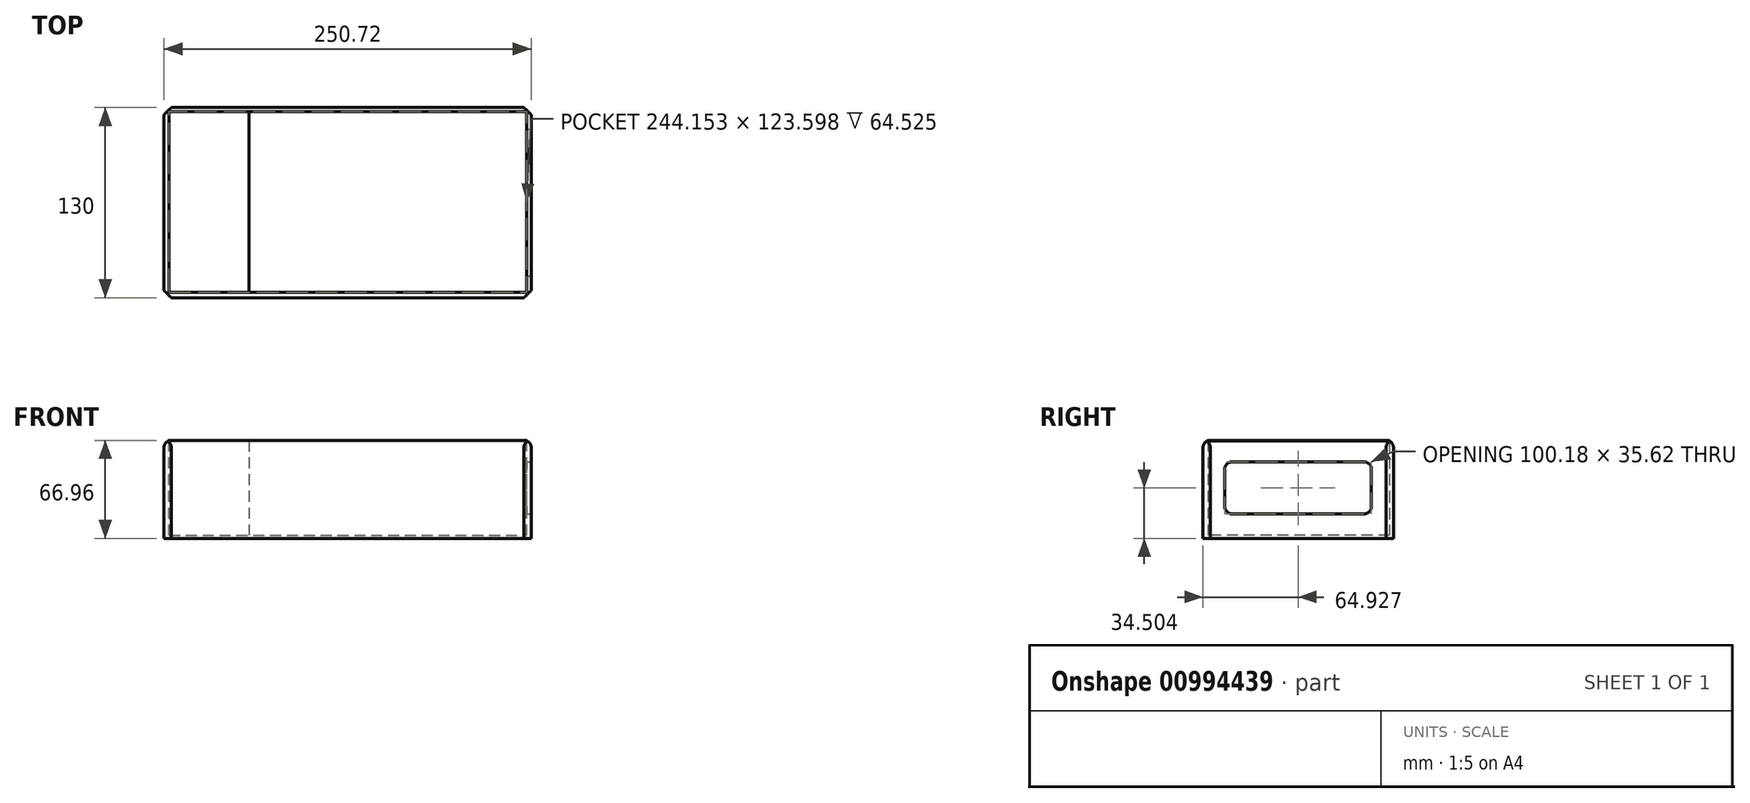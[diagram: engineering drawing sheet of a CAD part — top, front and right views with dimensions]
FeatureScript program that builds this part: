
annotation { "Feature Type Name" : "Feature", "Feature Type Description" : "" }
export const myFeature = defineFeature(function(context is Context, id is Id, definition is map)
    precondition{}
    {
        {
            var Q0;
            Q0=qCreatedBy(makeId("Front.planeOp"),FACE);
            var sketch = newSketch(context, id + "F0", { "sketchPlane" : qUnion([Q0])});
            skLineSegment(sketch, "E0.bottom", {"start": v(125.36, -33.53) * mm, "end": v(-125.36, -33.53) * mm});
            skLineSegment(sketch, "E0.top", {"start": v(125.36, 33.53) * mm, "end": v(-125.36, 33.53) * mm});
            skLineSegment(sketch, "E0.left", {"start": v(125.36, -33.53) * mm, "end": v(125.36, 33.53) * mm});
            skLineSegment(sketch, "E0.right", {"start": v(-125.36, -33.53) * mm, "end": v(-125.36, 33.53) * mm});
            skPoint(sketch, "E0.middle", {"position": v(0, 0) * mm});
            skSolve(sketch);
        }
        {
            var Q0;
            Q0 = qSketchRegion(id + "F0", true);
            extrude(context, id + "F1", {"entities" : qUnion([Q0]), "oppositeDirection" : true, "depth" : 130 * mm, "offsetDistance" : 25 * mm});
        }
        {
            var Q0;
            Q0=makeQuery(id+"F1.opExtrude","SWEPT_FACE",FACE,{"disambiguationData":[OSD([sQuery(id+"F0.wireOp",EDGE,"E0.top")])]});
            var sketch = newSketch(context, id + "F2", { "sketchPlane" : qUnion([Q0])});
            skLineSegment(sketch, "E1.bottom", {"start": v(-121.89, 127.33) * mm, "end": v(122.27, 127.33) * mm});
            skLineSegment(sketch, "E1.top", {"start": v(-121.89, 3.73) * mm, "end": v(122.27, 3.73) * mm});
            skLineSegment(sketch, "E1.left", {"start": v(-121.89, 127.33) * mm, "end": v(-121.89, 3.73) * mm});
            skLineSegment(sketch, "E1.right", {"start": v(122.27, 127.33) * mm, "end": v(122.27, 3.73) * mm});
            skSolve(sketch);
        }
        {
            var Q0;
            Q0 = qSketchRegion(id + "F2", true);
            extrude(context, id + "F3", {"entities" : qUnion([Q0]), "operationType" : NewBodyOperationType.REMOVE, "oppositeDirection" : true, "depth" : 65.1 * mm, "offsetDistance" : 25 * mm});
        }
        {
            var Q0;
            Q0=makeQuery(id+"F1.opExtrude","CAP_EDGE",EDGE,{"disambiguationData":[OSD([sQuery(id+"F0.wireOp",EDGE,"E0.right")])],"isStart":true});
            var Q1;
            Q1=makeQuery(id+"F1.opExtrude","CAP_EDGE",EDGE,{"disambiguationData":[OSD([sQuery(id+"F0.wireOp",EDGE,"E0.right")])],"isStart":false});
            var Q2;
            Q2=makeQuery(id+"F1.opExtrude","CAP_EDGE",EDGE,{"disambiguationData":[OSD([sQuery(id+"F0.wireOp",EDGE,"E0.left")])],"isStart":false});
            var Q3;
            Q3=makeQuery(id+"F1.opExtrude","CAP_EDGE",EDGE,{"disambiguationData":[OSD([sQuery(id+"F0.wireOp",EDGE,"E0.left")])],"isStart":true});
            chamfer(context, id + "F4", {"entities" : qUnion([Q0, Q1, Q2, Q3]), "width" : 5 * mm, "tangentPropagation" : true});
        }
        {
            var Q0;
            Q0=makeQuery(id+"F1.opExtrude","SWEPT_EDGE",EDGE,{"disambiguationData":[OSD([sQuery(id+"F0.wireOp",EDGE,"E0.top"),sQuery(id+"F0.wireOp",EDGE,"E0.right")])]});
            var Q1;
            Q1=makeQuery(id+"F1.opExtrude","CAP_EDGE",EDGE,{"disambiguationData":[OSD([sQuery(id+"F0.wireOp",EDGE,"E0.top")])],"isStart":false});
            var Q2;
            Q2=makeQuery(id+"F1.opExtrude","CAP_EDGE",EDGE,{"disambiguationData":[OSD([sQuery(id+"F0.wireOp",EDGE,"E0.top")])],"isStart":true});
            var Q3;
            Q3=makeQuery(id+"F1.opExtrude","SWEPT_EDGE",EDGE,{"disambiguationData":[OSD([sQuery(id+"F0.wireOp",EDGE,"E0.top"),sQuery(id+"F0.wireOp",EDGE,"E0.left")])]});
            fillet(context, id + "F5", {"entities" : qUnion([Q0, Q1, Q2, Q3]), "radius" : 5 * mm, "tangentPropagation" : true, "allowEdgeOverflow" : false});
        }
        {
            var Q0;
            Q0=makeQuery(id+"F1.opExtrude","SWEPT_FACE",FACE,{"disambiguationData":[OSD([sQuery(id+"F0.wireOp",EDGE,"E0.left")])]});
            var sketch = newSketch(context, id + "F6", { "sketchPlane" : qUnion([Q0])});
            skLineSegment(sketch, "E2.bottom", {"start": v(14.84, 18.78) * mm, "end": v(115.02, 18.78) * mm});
            skLineSegment(sketch, "E2.top", {"start": v(14.84, -16.84) * mm, "end": v(115.02, -16.84) * mm});
            skLineSegment(sketch, "E2.left", {"start": v(14.84, 18.78) * mm, "end": v(14.84, -16.84) * mm});
            skLineSegment(sketch, "E2.right", {"start": v(115.02, 18.78) * mm, "end": v(115.02, -16.84) * mm});
            skSolve(sketch);
        }
        {
            var Q0;
            Q0=makeQuery(id+"F6.imprint","IMPRINT",FACE,{"disambiguationData":[TD([[makeQuery(id+"F6.imprint","IMPRINT",EDGE,{"derivedFrom":sQuery(id+"F6.wireOp",EDGE,"E2.bottom")}),-1.0]])]});
            extrude(context, id + "F7", {"entities" : qUnion([Q0]), "operationType" : NewBodyOperationType.REMOVE, "oppositeDirection" : true, "depth" : 25 * mm, "offsetDistance" : 25 * mm});
        }
        {
            var Q0;
            Q0=makeQuery(id+"F7.boolean.opBoolean","COPY",EDGE,{"derivedFrom":makeQuery(id+"F7.opExtrude","SWEPT_EDGE",EDGE,{"disambiguationData":[OSD([sQuery(id+"F6.wireOp",EDGE,"E2.bottom"),sQuery(id+"F6.wireOp",EDGE,"E2.left")])]})});
            var Q1;
            Q1=makeQuery(id+"F7.boolean.opBoolean","COPY",EDGE,{"derivedFrom":makeQuery(id+"F7.opExtrude","SWEPT_EDGE",EDGE,{"disambiguationData":[OSD([sQuery(id+"F6.wireOp",EDGE,"E2.bottom"),sQuery(id+"F6.wireOp",EDGE,"E2.right")])]})});
            var Q2;
            Q2=makeQuery(id+"F7.boolean.opBoolean","COPY",EDGE,{"derivedFrom":makeQuery(id+"F7.opExtrude","SWEPT_EDGE",EDGE,{"disambiguationData":[OSD([sQuery(id+"F6.wireOp",EDGE,"E2.top"),sQuery(id+"F6.wireOp",EDGE,"E2.right")])]})});
            var Q3;
            Q3=makeQuery(id+"F7.boolean.opBoolean","COPY",EDGE,{"derivedFrom":makeQuery(id+"F7.opExtrude","SWEPT_EDGE",EDGE,{"disambiguationData":[OSD([sQuery(id+"F6.wireOp",EDGE,"E2.top"),sQuery(id+"F6.wireOp",EDGE,"E2.left")])]})});
            fillet(context, id + "F8", {"entities" : qUnion([Q0, Q1, Q2, Q3]), "radius" : 5 * mm, "tangentPropagation" : true, "allowEdgeOverflow" : false});
        }
        {
            var Q0;
            Q0=makeQuery(id+"F3.boolean.opBoolean","COPY",FACE,{"derivedFrom":makeQuery(id+"F3.opExtrude","CAP_FACE",FACE,{"disambiguationData":[OSD([sQuery(id+"F2.wireOp",EDGE,"E1.bottom"),sQuery(id+"F2.wireOp",EDGE,"E1.top"),sQuery(id+"F2.wireOp",EDGE,"E1.left"),sQuery(id+"F2.wireOp",EDGE,"E1.right")])],"isStart":false})});
            var sketch = newSketch(context, id + "F9", { "sketchPlane" : qUnion([Q0])});
            skLineSegment(sketch, "E3.bottom", {"start": v(-121.89, 127.33) * mm, "end": v(-67.31, 127.33) * mm});
            skLineSegment(sketch, "E3.top", {"start": v(-121.89, 3.73) * mm, "end": v(-67.31, 3.73) * mm});
            skLineSegment(sketch, "E3.left", {"start": v(-121.89, 127.33) * mm, "end": v(-121.89, 3.73) * mm});
            skLineSegment(sketch, "E3.right", {"start": v(-67.31, 127.33) * mm, "end": v(-67.31, 3.73) * mm});
            skSolve(sketch);
        }
        {
            var Q0;
            Q0=makeQuery(id+"F9.imprint","IMPRINT",FACE,{"disambiguationData":[TD([[makeQuery(id+"F9.imprint","IMPRINT",EDGE,{"derivedFrom":sQuery(id+"F9.wireOp",EDGE,"E3.bottom")}),-1.0]])]});
            extrude(context, id + "F10", {"entities" : qUnion([Q0]), "depth" : 65 * mm, "offsetDistance" : 25 * mm});
        }
    });
